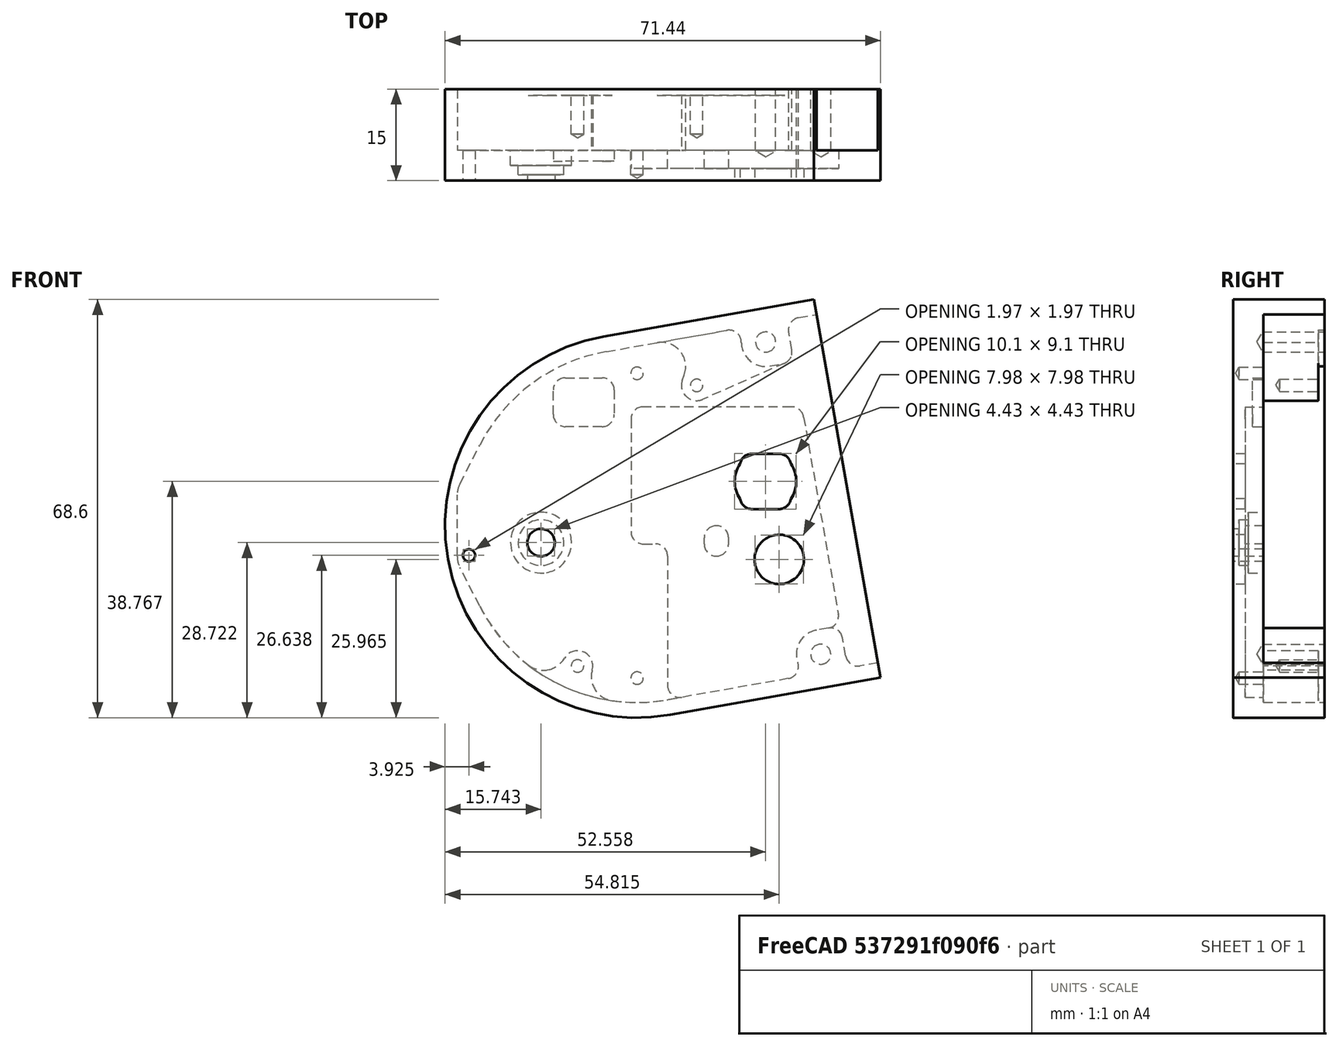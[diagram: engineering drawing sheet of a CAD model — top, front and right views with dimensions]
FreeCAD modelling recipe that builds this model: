
FCSTD DOCUMENT  (FreeCAD 1.1R20260414 (Git shallow))
Label: Mounting Box
License: All rights reserved
LicenseURL: https://en.wikipedia.org/wiki/All_rights_reserved
objects: Part::Feature×1, App::Point×1, Sketcher::SketchObject×1, PartDesign::Body×1
note: 4 computed .brp shape members not serialized (recipe doc carries the construction recipe); baked Part::Feature solids carry a one-line shape summary decoded from their .brp

FEATURE [Part::Feature] Part__Feature  label="ARADMINICAP TCF LEG CONTROL MODULE - SIDE MOUNT HOUSING TOP"
  Placement = pos=(0,0,0) rot=(0,-1,0;0.174533rad)
  shape: bbox 71.44 x 15 x 68.6 mm, 117 faces (baked)
FEATURE [App::Point] Origin001
  Role = Origin
FEATURE [Sketcher::SketchObject] Sketch
  ArcFitTolerance = 1e-06
  AttachmentSupport = -> [Origin]
  ExternalTypes = [0]
  FullyConstrained = true
  MakeInternals = false
  MapMode = 5
  Placement = pos=(0,0,0) rot=(1,0,0;1.5708rad)
  _ExternalGeoVersion = 1
FEATURE [PartDesign::Body] Body
  AllowCompound = true
  Group = -> [Sketch]
  Origin = -> Origin
